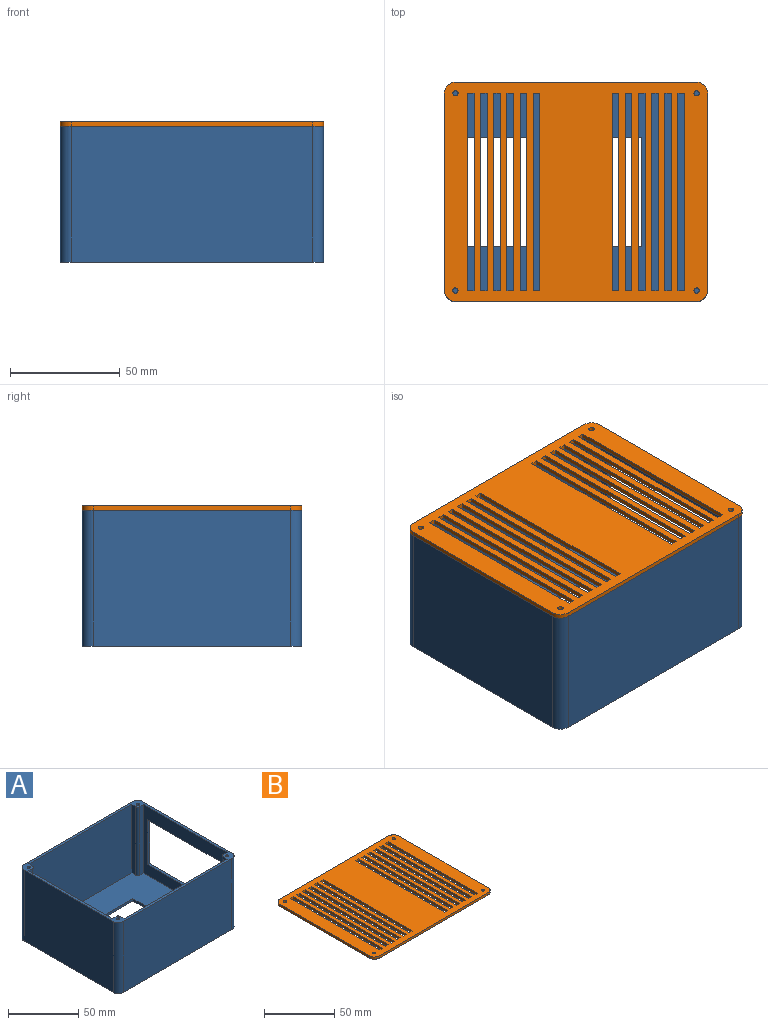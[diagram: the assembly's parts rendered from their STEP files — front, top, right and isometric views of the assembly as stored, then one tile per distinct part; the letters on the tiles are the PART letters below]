
ASSEMBLY  parts=2 mates=1
PART A: 47 faces, bbox 120x100x62 mm
  f0: plane 90x62mm, normal (1,0,0), area 2616mm2, adj f3,f17,f18,f38,f43,f44,f45,f46
  f1: plane 84x60mm, normal (-1,0,0), area 2076mm2, adj f2,f26,f27,f38,f43,f44,f45,f46
  f2: plane 116x96mm, normal (0,0,1), area 7995.4mm2, adj f1,f9,f10,f11,f12,f13,f14,f15
  f3: cylinder r=5mm len=62mm, axis (0,0,-1), area 486.9mm2, adj f0,f4,f18,f38
  f4: plane 110x62mm, normal (0,1,0), area 6820mm2, adj f3,f5,f18,f38
  f5: cylinder r=5mm len=62mm, axis (0,0,-1), area 486.9mm2, adj f4,f6,f18,f38
  f6: plane 90x62mm, normal (-1,0,0), area 5580mm2, adj f5,f7,f18,f38
  f7: cylinder r=5mm len=62mm, axis (0,0,-1), area 486.9mm2, adj f6,f8,f18,f38
  f8: plane 110x62mm, normal (0,-1,0), area 6820mm2, adj f7,f17,f18,f38
  f9: plane 50x2mm, normal (1,0,0), area 100mm2, adj f2,f10,f15,f18
  f10: plane 30x2mm, normal (0,-1,0), area 60mm2, adj f2,f9,f11,f18
  f11: plane 50x2mm, normal (-1,0,0), area 100mm2, adj f2,f10,f15,f18
  f12: plane 50x2mm, normal (1,0,0), area 100mm2, adj f2,f13,f16,f18
  f13: plane 30x2mm, normal (0,-1,0), area 60mm2, adj f2,f12,f14,f18
  f14: plane 50x2mm, normal (-1,0,0), area 100mm2, adj f2,f13,f16,f18
  f15: plane 30x2mm, normal (0,1,0), area 60mm2, adj f2,f9,f11,f18
  f16: plane 30x2mm, normal (0,1,0), area 60mm2, adj f2,f12,f14,f18
  f17: cylinder r=5mm len=62mm, axis (0,0,-1), area 486.9mm2, adj f0,f8,f18,f38
  f18: plane 120x100mm, normal (0,0,-1), area 8978.5mm2, adj f0,f3,f4,f5,f6,f7,f8,f9
  f19: plane 84x60mm, normal (1,0,0), area 5040mm2, adj f2,f20,f37,f38
  f20: plane 60x4mm, normal (0,-1,0), area 240mm2, adj f2,f19,f21,f38
  f21: cylinder r=2mm len=60mm, axis (0,0,-1), area 188.5mm2, adj f2,f20,f22,f38
  f22: plane 60x4mm, normal (1,0,0), area 240mm2, adj f2,f21,f23,f38
  f23: plane 104x60mm, normal (0,-1,0), area 6240mm2, adj f2,f22,f24,f38
  f24: plane 60x4mm, normal (-1,0,0), area 240mm2, adj f2,f23,f25,f38
  f25: cylinder r=2mm len=60mm, axis (0,0,-1), area 188.5mm2, adj f2,f24,f26,f38
  f26: plane 60x4mm, normal (0,-1,0), area 240mm2, adj f1,f2,f25,f38
  f27: plane 60x4mm, normal (0,1,0), area 240mm2, adj f1,f2,f28,f38
  f28: cylinder r=2mm len=60mm, axis (0,0,-1), area 188.5mm2, adj f2,f27,f29,f38
  f29: plane 60x4mm, normal (-1,0,0), area 240mm2, adj f2,f28,f30,f38
  f30: plane 104x60mm, normal (0,1,0), area 6240mm2, adj f2,f29,f31,f38
  f31: plane 60x4mm, normal (1,0,0), area 240mm2, adj f2,f30,f32,f38
  f32: cylinder r=2mm len=60mm, axis (0,0,-1), area 188.5mm2, adj f2,f31,f37,f38
  f33: cylinder r=1.2mm len=60mm, axis (0,0,-1), area 452.4mm2, adj f38,f39
  f34: cylinder r=1.2mm len=60mm, axis (0,0,-1), area 452.4mm2, adj f38,f40
  f35: cylinder r=1.2mm len=60mm, axis (0,0,-1), area 452.4mm2, adj f38,f41
  f36: cylinder r=1.2mm len=60mm, axis (0,0,-1), area 452.4mm2, adj f38,f42
  f37: plane 60x4mm, normal (0,1,0), area 240mm2, adj f2,f19,f32,f38
  f38: plane 120x100mm, normal (0,0,1), area 965mm2, adj f0,f1,f3,f4,f5,f6,f7,f8
  f39: plane 2.4x2.4mm, normal (0,0,1), area 4.5mm2, adj f33
  f40: plane 2.4x2.4mm, normal (0,0,1), area 4.5mm2, adj f34
  f41: plane 2.4x2.4mm, normal (0,0,1), area 4.5mm2, adj f35
  f42: plane 2.4x2.4mm, normal (0,0,1), area 4.5mm2, adj f36
  f43: plane 76x2mm, normal (0,0,-1), area 152mm2, adj f0,f1,f44,f46
  f44: plane 39x2mm, normal (0,1,0), area 78mm2, adj f0,f1,f43,f45
  f45: plane 76x2mm, normal (0,0,1), area 152mm2, adj f0,f1,f44,f46
  f46: plane 39x2mm, normal (0,-1,0), area 78mm2, adj f0,f1,f43,f45
PART B: 62 faces, bbox 120x100x2 mm
  f0: plane 90x2mm, normal (1,0,0), area 180mm2, adj f1,f46,f60,f61
  f1: plane 3x2mm, normal (0,-1,0), area 6mm2, adj f0,f2,f60,f61
  f2: plane 90x2mm, normal (-1,0,0), area 180mm2, adj f1,f46,f60,f61
  f3: plane 90x2mm, normal (1,0,0), area 180mm2, adj f4,f47,f60,f61
  f4: plane 3x2mm, normal (0,-1,0), area 6mm2, adj f3,f5,f60,f61
  f5: plane 90x2mm, normal (-1,0,0), area 180mm2, adj f4,f47,f60,f61
  f6: plane 90x2mm, normal (1,0,0), area 180mm2, adj f7,f48,f60,f61
  f7: plane 3x2mm, normal (0,-1,0), area 6mm2, adj f6,f8,f60,f61
  f8: plane 90x2mm, normal (-1,0,0), area 180mm2, adj f7,f48,f60,f61
  f9: plane 90x2mm, normal (1,0,0), area 180mm2, adj f10,f49,f60,f61
  f10: plane 3x2mm, normal (0,-1,0), area 6mm2, adj f9,f11,f60,f61
  f11: plane 90x2mm, normal (-1,0,0), area 180mm2, adj f10,f49,f60,f61
  f12: plane 90x2mm, normal (1,0,0), area 180mm2, adj f13,f50,f60,f61
  f13: plane 3x2mm, normal (0,-1,0), area 6mm2, adj f12,f14,f60,f61
  f14: plane 90x2mm, normal (-1,0,0), area 180mm2, adj f13,f50,f60,f61
  f15: plane 90x2mm, normal (1,0,0), area 180mm2, adj f16,f51,f60,f61
  f16: plane 3x2mm, normal (0,-1,0), area 6mm2, adj f15,f17,f60,f61
  f17: plane 90x2mm, normal (-1,0,0), area 180mm2, adj f16,f51,f60,f61
  f18: plane 90x2mm, normal (1,0,0), area 180mm2, adj f19,f52,f60,f61
  f19: plane 3x2mm, normal (0,-1,0), area 6mm2, adj f18,f20,f60,f61
  f20: plane 90x2mm, normal (-1,0,0), area 180mm2, adj f19,f52,f60,f61
  f21: plane 90x2mm, normal (1,0,0), area 180mm2, adj f22,f53,f60,f61
  f22: plane 3x2mm, normal (0,-1,0), area 6mm2, adj f21,f23,f60,f61
  f23: plane 90x2mm, normal (-1,0,0), area 180mm2, adj f22,f53,f60,f61
  f24: plane 90x2mm, normal (1,0,0), area 180mm2, adj f25,f54,f60,f61
  f25: plane 3x2mm, normal (0,-1,0), area 6mm2, adj f24,f26,f60,f61
  f26: plane 90x2mm, normal (-1,0,0), area 180mm2, adj f25,f54,f60,f61
  f27: plane 90x2mm, normal (1,0,0), area 180mm2, adj f28,f55,f60,f61
  f28: plane 3x2mm, normal (0,-1,0), area 6mm2, adj f27,f29,f60,f61
  f29: plane 90x2mm, normal (-1,0,0), area 180mm2, adj f28,f55,f60,f61
  f30: plane 90x2mm, normal (1,0,0), area 180mm2, adj f31,f56,f60,f61
  f31: plane 3x2mm, normal (0,-1,0), area 6mm2, adj f30,f32,f60,f61
  f32: plane 90x2mm, normal (-1,0,0), area 180mm2, adj f31,f56,f60,f61
  f33: plane 90x2mm, normal (1,0,0), area 180mm2, adj f34,f57,f60,f61
  f34: plane 3x2mm, normal (0,-1,0), area 6mm2, adj f33,f35,f60,f61
  f35: plane 90x2mm, normal (-1,0,0), area 180mm2, adj f34,f57,f60,f61
  f36: plane 110x2mm, normal (0,1,0), area 220mm2, adj f37,f58,f60,f61
  f37: cylinder r=5mm len=5mm, axis (0,0,-1), area 15.7mm2, adj f36,f38,f60,f61
  f38: plane 90x2mm, normal (-1,0,0), area 180mm2, adj f37,f39,f60,f61
  f39: cylinder r=5mm len=5mm, axis (0,0,-1), area 15.7mm2, adj f38,f40,f60,f61
  f40: plane 110x2mm, normal (0,-1,0), area 220mm2, adj f39,f41,f60,f61
  f41: cylinder r=5mm len=5mm, axis (0,0,-1), area 15.7mm2, adj f40,f42,f60,f61
  f42: plane 90x2mm, normal (1,0,0), area 180mm2, adj f41,f58,f60,f61
  f43: cylinder r=1.2mm len=2.4mm, axis (0,0,-1), area 15.1mm2, adj f60,f61
  f44: cylinder r=1.2mm len=2.4mm, axis (0,0,-1), area 15.1mm2, adj f60,f61
  f45: cylinder r=1.2mm len=2.4mm, axis (0,0,-1), area 15.1mm2, adj f60,f61
  f46: plane 3x2mm, normal (0,1,0), area 6mm2, adj f0,f2,f60,f61
  f47: plane 3x2mm, normal (0,1,0), area 6mm2, adj f3,f5,f60,f61
  f48: plane 3x2mm, normal (0,1,0), area 6mm2, adj f6,f8,f60,f61
  f49: plane 3x2mm, normal (0,1,0), area 6mm2, adj f9,f11,f60,f61
  f50: plane 3x2mm, normal (0,1,0), area 6mm2, adj f12,f14,f60,f61
  f51: plane 3x2mm, normal (0,1,0), area 6mm2, adj f15,f17,f60,f61
  f52: plane 3x2mm, normal (0,1,0), area 6mm2, adj f18,f20,f60,f61
  f53: plane 3x2mm, normal (0,1,0), area 6mm2, adj f21,f23,f60,f61
  f54: plane 3x2mm, normal (0,1,0), area 6mm2, adj f24,f26,f60,f61
  f55: plane 3x2mm, normal (0,1,0), area 6mm2, adj f27,f29,f60,f61
  f56: plane 3x2mm, normal (0,1,0), area 6mm2, adj f30,f32,f60,f61
  f57: plane 3x2mm, normal (0,1,0), area 6mm2, adj f33,f35,f60,f61
  f58: cylinder r=5mm len=5mm, axis (0,0,-1), area 15.7mm2, adj f36,f42,f60,f61
  f59: cylinder r=1.2mm len=2.4mm, axis (0,0,-1), area 15.1mm2, adj f60,f61
  f60: plane 120x100mm, normal (0,0,1), area 8720.4mm2, adj f0,f1,f2,f3,f4,f5,f6,f7
  f61: plane 120x100mm, normal (0,0,-1), area 8720.4mm2, adj f0,f1,f2,f3,f4,f5,f6,f7
PLACE A at identity
PLACE B t=(160.45,0,62)mm
MATE fastened B.f41 <-> A.f17  axis (0,0,-1) through (115,-95,62)mm
